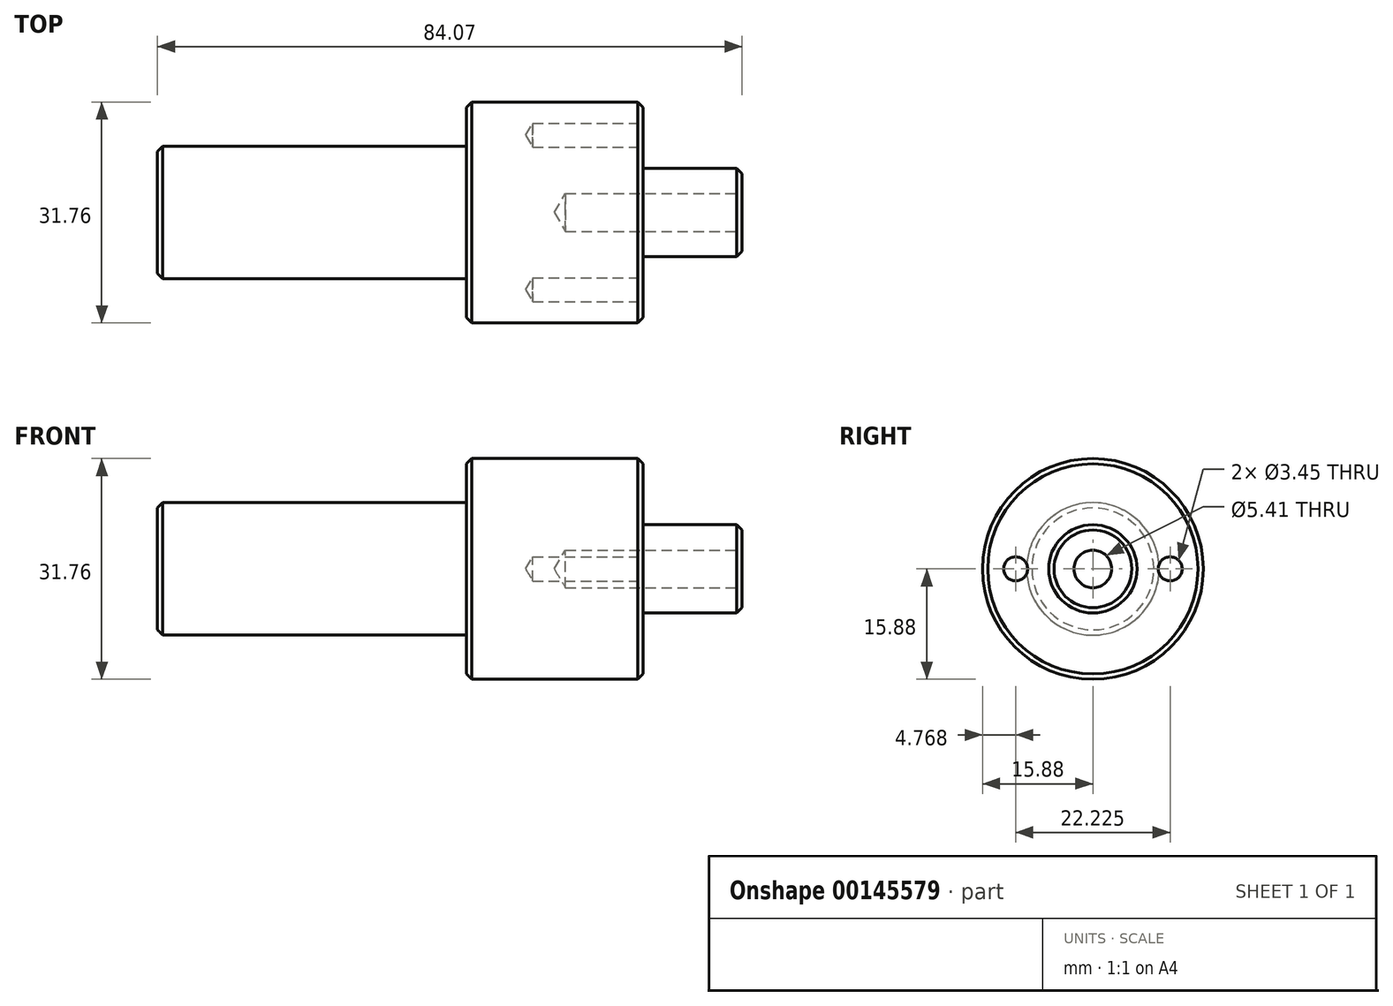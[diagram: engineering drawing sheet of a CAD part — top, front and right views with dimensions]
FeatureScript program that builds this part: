
annotation { "Feature Type Name" : "Feature", "Feature Type Description" : "" }
export const myFeature = defineFeature(function(context is Context, id is Id, definition is map)
    precondition{}
    {
        {
            var Q0;
            Q0=qCreatedBy(makeId("Top.planeOp"),FACE);
            var sketch = newSketch(context, id + "F0", { "sketchPlane" : qUnion([Q0])});
            skLineSegment(sketch, "E0", {"start": v(0, 0) * mm, "end": v(0, 6.35) * mm});
            skLineSegment(sketch, "E1", {"start": v(0, 6.35) * mm, "end": v(-14.22, 6.35) * mm});
            skLineSegment(sketch, "E2", {"start": v(-14.22, 6.35) * mm, "end": v(-14.22, 15.87) * mm});
            skLineSegment(sketch, "E3", {"start": v(-14.22, 15.87) * mm, "end": v(-39.62, 15.87) * mm});
            skLineSegment(sketch, "E4", {"start": v(-39.62, 15.87) * mm, "end": v(-39.62, 9.53) * mm});
            skLineSegment(sketch, "E5", {"start": v(-39.62, 9.53) * mm, "end": v(-84.07, 9.52) * mm});
            skLineSegment(sketch, "E6", {"start": v(-84.07, 9.52) * mm, "end": v(-84.07, 0) * mm});
            skLineSegment(sketch, "E7", {"start": v(-84.07, 0) * mm, "end": v(0, 0) * mm});
            skSolve(sketch);
        }
        {
            var Q0;
            Q0=makeQuery(id+"F0.imprint","IMPRINT",FACE,{"disambiguationData":[TD([[makeQuery(id+"F0.imprint","IMPRINT",EDGE,{"derivedFrom":sQuery(id+"F0.wireOp",EDGE,"E0")}),1.0]])]});
            var Q1;
            Q1=sQuery(id+"F0.wireOp",EDGE,"E7");
            revolve(context, id + "F1", {"entities" : qUnion([Q0]), "axis" : qUnion([Q1]), "revolveType" : RevolveType.FULL});
        }
        {
            var Q0;
            Q0=makeQuery(id+"F1.opRevolve","SWEPT_FACE",FACE,{"disambiguationData":[OSD([sQuery(id+"F0.wireOp",EDGE,"E0")])]});
            var sketch = newSketch(context, id + "F2", { "sketchPlane" : qUnion([Q0])});
            skCircle(sketch, "E8", {"center": v(0, 0) * mm, "radius": 3.74 * mm});
            skSolve(sketch);
        }
        {
            var Q0;
            Q0=sQuery(id+"F2.wireOp",VERTEX,"E8.center");
            var Q1;
            Q1=makeQuery(id+"F1.opRevolve","SWEPT_BODY",BODY,{"disambiguationData":[OSD([sQuery(id+"F0.wireOp",EDGE,"E0"),sQuery(id+"F0.wireOp",EDGE,"E1"),sQuery(id+"F0.wireOp",EDGE,"E2"),sQuery(id+"F0.wireOp",EDGE,"E3"),sQuery(id+"F0.wireOp",EDGE,"E4"),sQuery(id+"F0.wireOp",EDGE,"E5"),sQuery(id+"F0.wireOp",EDGE,"E6"),sQuery(id+"F0.wireOp",EDGE,"E7")])]});
            hole(context, id + "F3", {"style" : HoleStyle.SIMPLE, "endStyle" : HoleEndStyle.BLIND, "standardTappedOrClearance" : lookupTablePath({ "standard" : "ANSI", "engagement" : "75%", "pitch" : "28 tpi", "size" : "1/4", "type" : "Tapped" }), "standardBlindInLast" : lookupTablePath({ "standard" : "ANSI", "engagement" : "75%", "pitch" : "28 tpi", "size" : "1/4", "type" : "Tapped" }), "holeDiameter" : 5.4 * mm, "holeDepth" : 25.4 * mm, "locations" : qUnion([Q0]), "scope" : qUnion([Q1]), "majorDiameter" : 6.35 * mm});
        }
        {
            var Q0;
            Q0=makeQuery(id+"F1.opRevolve","SWEPT_FACE",FACE,{"disambiguationData":[OSD([sQuery(id+"F0.wireOp",EDGE,"E2")])]});
            var sketch = newSketch(context, id + "F4", { "sketchPlane" : qUnion([Q0])});
            skCircle(sketch, "E9", {"center": v(-11.11, 0) * mm, "radius": 3.35 * mm});
            skCircle(sketch, "E10.MirrorC", {"center": v(11.11, 0) * mm, "radius": 3.35 * mm});
            skSolve(sketch);
        }
        {
            var Q0;
            Q0=sQuery(id+"F4.wireOp",VERTEX,"E9.center");
            var Q1;
            Q1=sQuery(id+"F4.wireOp",VERTEX,"E10.MirrorC.center");
            var Q2;
            Q2=makeQuery(id+"F1.opRevolve","SWEPT_BODY",BODY,{"disambiguationData":[OSD([sQuery(id+"F0.wireOp",EDGE,"E0"),sQuery(id+"F0.wireOp",EDGE,"E1"),sQuery(id+"F0.wireOp",EDGE,"E2"),sQuery(id+"F0.wireOp",EDGE,"E3"),sQuery(id+"F0.wireOp",EDGE,"E4"),sQuery(id+"F0.wireOp",EDGE,"E5"),sQuery(id+"F0.wireOp",EDGE,"E6"),sQuery(id+"F0.wireOp",EDGE,"E7")])]});
            hole(context, id + "F5", {"style" : HoleStyle.SIMPLE, "endStyle" : HoleEndStyle.BLIND, "standardTappedOrClearance" : lookupTablePath({ "standard" : "ANSI", "engagement" : "75%", "pitch" : "32 tpi", "size" : "#8", "type" : "Tapped" }), "standardBlindInLast" : lookupTablePath({ "standard" : "ANSI", "engagement" : "75%", "pitch" : "32 tpi", "size" : "#8", "type" : "Tapped" }), "holeDiameter" : 3.45 * mm, "holeDepth" : 15.88 * mm, "locations" : qUnion([Q0, Q1]), "scope" : qUnion([Q2]), "majorDiameter" : 4.17 * mm});
        }
        {
            var Q0;
            Q0=makeQuery(id+"F1.opRevolve","SWEPT_EDGE",EDGE,{"disambiguationData":[OSD([sQuery(id+"F0.wireOp",EDGE,"E0"),sQuery(id+"F0.wireOp",EDGE,"E1")])]});
            var Q1;
            Q1=makeQuery(id+"F1.opRevolve","SWEPT_EDGE",EDGE,{"disambiguationData":[OSD([sQuery(id+"F0.wireOp",EDGE,"E2"),sQuery(id+"F0.wireOp",EDGE,"E3")])]});
            var Q2;
            Q2=makeQuery(id+"F1.opRevolve","SWEPT_EDGE",EDGE,{"disambiguationData":[OSD([sQuery(id+"F0.wireOp",EDGE,"E3"),sQuery(id+"F0.wireOp",EDGE,"E4")])]});
            var Q3;
            Q3=makeQuery(id+"F1.opRevolve","SWEPT_EDGE",EDGE,{"disambiguationData":[OSD([sQuery(id+"F0.wireOp",EDGE,"E5"),sQuery(id+"F0.wireOp",EDGE,"E6")])]});
            chamfer(context, id + "F6", {"entities" : qUnion([Q0, Q1, Q2, Q3]), "width" : 0.76 * mm, "tangentPropagation" : true});
        }
    });
